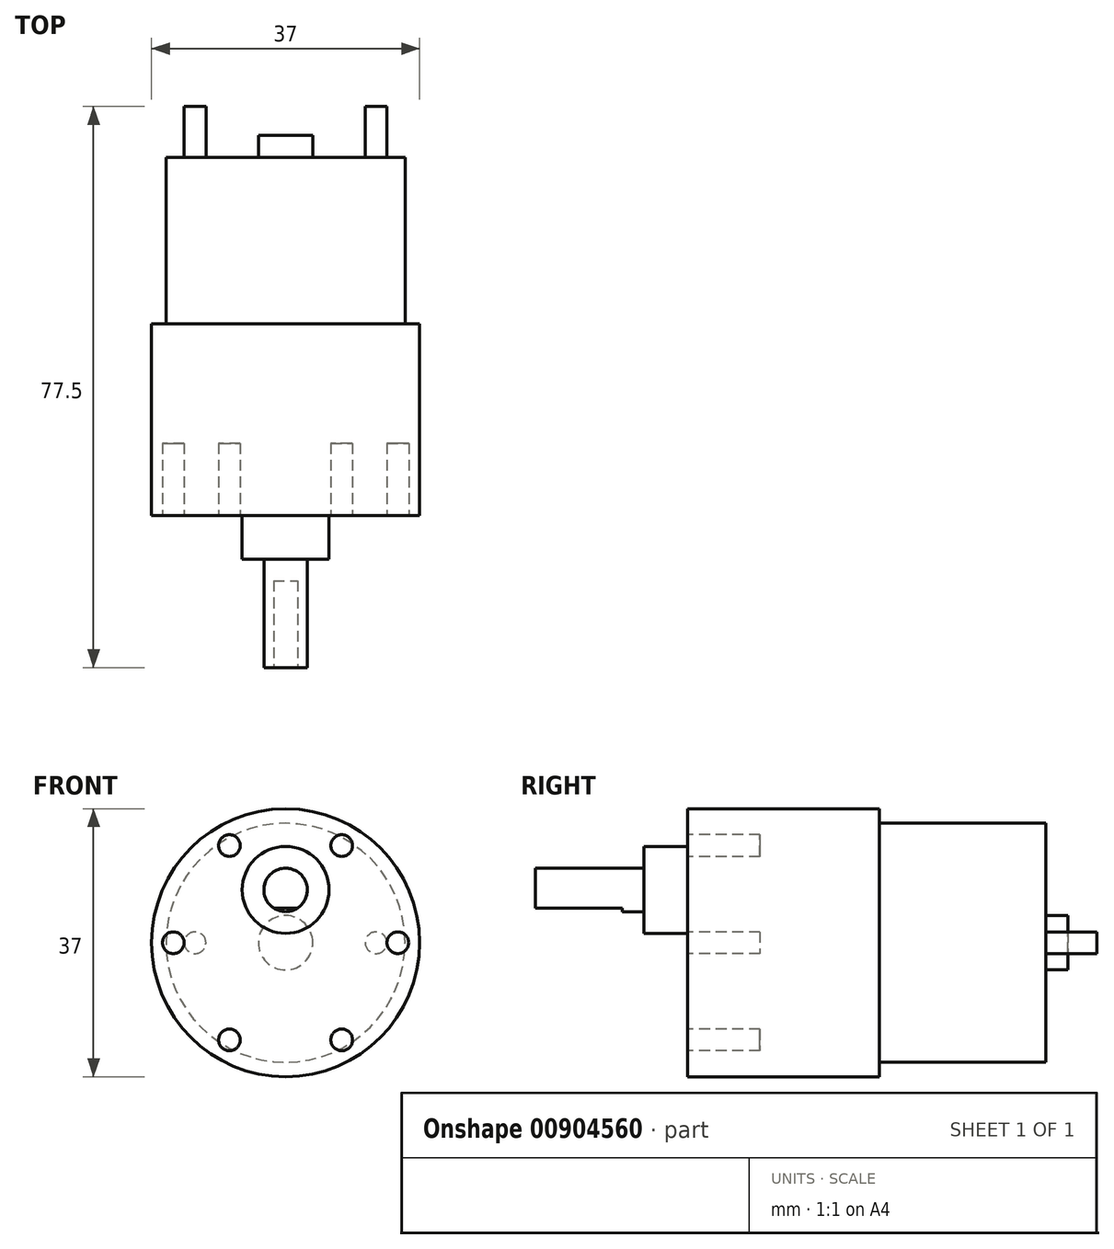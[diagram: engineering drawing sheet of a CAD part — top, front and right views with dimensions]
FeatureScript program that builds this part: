
annotation { "Feature Type Name" : "Feature", "Feature Type Description" : "" }
export const myFeature = defineFeature(function(context is Context, id is Id, definition is map)
    precondition{}
    {
        {
            var Q0;
            Q0=qCreatedBy(makeId("Front.planeOp"),FACE);
            var sketch = newSketch(context, id + "F0", { "sketchPlane" : qUnion([Q0])});
            skCircle(sketch, "E0", {"center": v(0, 0) * mm, "radius": 16.5 * mm});
            skCircle(sketch, "E1", {"center": v(0, 0) * mm, "radius": 18.5 * mm});
            skSolve(sketch);
        }
        {
            var Q0;
            Q0 = qSketchRegion(id + "F0", true);
            var Q1;
            Q1=makeQuery(id+"F0.imprint","IMPRINT",FACE,{"disambiguationData":[TD([[makeQuery(id+"F0.imprint","IMPRINT",EDGE,{"derivedFrom":sQuery(id+"F0.wireOp",EDGE,"E0")}),1.0]])]});
            extrude(context, id + "F1", {"entities" : qUnion([Q0, Q1]), "depth" : 26.5 * mm, "offsetDistance" : 25 * mm});
        }
        {
            var Q0;
            Q0=makeQuery(id+"F0.imprint","IMPRINT",FACE,{"disambiguationData":[TD([[makeQuery(id+"F0.imprint","IMPRINT",EDGE,{"derivedFrom":sQuery(id+"F0.wireOp",EDGE,"E0")}),1.0]])]});
            extrude(context, id + "F2", {"entities" : qUnion([Q0]), "operationType" : NewBodyOperationType.ADD, "oppositeDirection" : true, "depth" : 23 * mm, "offsetDistance" : 25 * mm});
        }
        {
            var Q0;
            Q0=makeQuery(id+"F1.opExtrude","CAP_FACE",FACE,{"disambiguationData":[OSD([sQuery(id+"F0.wireOp",EDGE,"E1")])],"isStart":false});
            var sketch = newSketch(context, id + "F3", { "sketchPlane" : qUnion([Q0])});
            skCircle(sketch, "E2", {"center": v(0, 7.3) * mm, "radius": 6 * mm});
            skCircle(sketch, "E3", {"center": v(0, 7.3) * mm, "radius": 3 * mm});
            skPoint(sketch, "E4", {"position": v(0, 1.3) * mm});
            skCircle(sketch, "E5", {"center": v(-15.5, 0) * mm, "radius": 1.5 * mm});
            skSolve(sketch);
        }
        {
            var Q0;
            Q0=makeQuery(id+"F3.imprint","IMPRINT",FACE,{"disambiguationData":[TD([[makeQuery(id+"F3.imprint","IMPRINT",EDGE,{"derivedFrom":sQuery(id+"F3.wireOp",EDGE,"E2")}),1.0]])]});
            extrude(context, id + "F4", {"entities" : qUnion([Q0]), "operationType" : NewBodyOperationType.ADD, "depth" : 6 * mm, "offsetDistance" : 25 * mm});
        }
        {
            var Q0;
            Q0=makeQuery(id+"F4.boolean.opBoolean","SPLIT",FACE,{"disambiguationData":[TD([makeQuery(id+"F4.opExtrude","SWEPT_FACE",FACE,{"disambiguationData":[OSD([sQuery(id+"F3.wireOp",EDGE,"E3")])]})])],"derivedFrom":makeQuery(id+"F1.opExtrude","CAP_FACE",FACE,{"disambiguationData":[OSD([sQuery(id+"F0.wireOp",EDGE,"E1")])],"isStart":false})});
            extrude(context, id + "F5", {"entities" : qUnion([Q0]), "operationType" : NewBodyOperationType.ADD, "depth" : 21 * mm, "offsetDistance" : 25 * mm});
        }
        {
            var Q0;
            Q0=makeQuery(id+"F5.opExtrude","CAP_FACE",FACE,{"disambiguationData":[OSD([sQuery(id+"F0.wireOp",EDGE,"E1")])],"isStart":false});
            var sketch = newSketch(context, id + "F6", { "sketchPlane" : qUnion([Q0])});
            skLineSegment(sketch, "E6", {"start": v(-1.66, 4.8) * mm, "end": v(1.66, 4.8) * mm});
            skArc(sketch, "E7", {"start": v(-1.66, 4.8) * mm, "mid": v(0, 4.3) * mm, "end": v(1.66, 4.8) * mm});
            skSolve(sketch);
        }
        {
            var Q0;
            Q0=makeQuery(id+"F6.imprint","IMPRINT",FACE,{"disambiguationData":[TD([[makeQuery(id+"F6.imprint","IMPRINT",EDGE,{"derivedFrom":sQuery(id+"F6.wireOp",EDGE,"E6")}),-1.0]])]});
            extrude(context, id + "F7", {"entities" : qUnion([Q0]), "operationType" : NewBodyOperationType.REMOVE, "oppositeDirection" : true, "depth" : 12 * mm, "offsetDistance" : 25 * mm});
        }
        {
            var Q0;
            Q0=makeQuery(id+"F3.imprint","IMPRINT",FACE,{"disambiguationData":[TD([[makeQuery(id+"F3.imprint","IMPRINT",EDGE,{"derivedFrom":sQuery(id+"F3.wireOp",EDGE,"E5")}),1.0]])]});
            var Q1;
            Q1=sQuery(id+"F3.wireOp",EDGE,"E5");
            extrude(context, id + "F8", {"entities" : qUnion([Q0]), "surfaceEntities" : qUnion([Q1]), "oppositeDirection" : true, "depth" : 10 * mm, "offsetDistance" : 25 * mm});
        }
        {
            var Q0;
            Q0=qCreatedBy(makeId("Right.planeOp"),FACE);
            var sketch = newSketch(context, id + "F9", { "sketchPlane" : qUnion([Q0])});
            skLineSegment(sketch, "E8", {"start": v(-66.54, 0) * mm, "end": v(54.78, 0) * mm, "construction": true});
            skSolve(sketch);
        }
        {
            var Q0;
            Q0=makeQuery(id+"F8.opExtrude","SWEPT_BODY",BODY,{"disambiguationData":[OSD([sQuery(id+"F3.wireOp",EDGE,"E5")])]});
            var Q1;
            Q1=sQuery(id+"F9.wireOp",EDGE,"E8");
            circularPattern(context, id + "F10", {"operationType" : NewBodyOperationType.REMOVE, "entities" : qUnion([Q0]), "axis" : qUnion([Q1]), "angle" : 360 * degree, "instanceCount" : 6, "equalSpace" : true});
        }
        {
            var Q0;
            Q0=makeQuery(id+"F2.opExtrude","CAP_FACE",FACE,{"disambiguationData":[OSD([sQuery(id+"F0.wireOp",EDGE,"E0")])],"isStart":false});
            var sketch = newSketch(context, id + "F11", { "sketchPlane" : qUnion([Q0])});
            skCircle(sketch, "E9", {"center": v(0, 0) * mm, "radius": 3.75 * mm});
            skCircle(sketch, "E10", {"center": v(-12.5, 0) * mm, "radius": 1.5 * mm});
            skCircle(sketch, "E11", {"center": v(12.5, 0) * mm, "radius": 1.5 * mm});
            skSolve(sketch);
        }
        {
            var Q0;
            Q0 = qSketchRegion(id + "F11", true);
            extrude(context, id + "F12", {"entities" : qUnion([Q0]), "operationType" : NewBodyOperationType.ADD, "depth" : 3 * mm, "offsetDistance" : 25 * mm});
        }
        {
            var Q0;
            Q0=makeQuery(id+"F11.imprint","IMPRINT",FACE,{"disambiguationData":[TD([[makeQuery(id+"F11.imprint","IMPRINT",EDGE,{"derivedFrom":sQuery(id+"F11.wireOp",EDGE,"E10")}),1.0]])]});
            var Q1;
            Q1=makeQuery(id+"F11.imprint","IMPRINT",FACE,{"disambiguationData":[TD([[makeQuery(id+"F11.imprint","IMPRINT",EDGE,{"derivedFrom":sQuery(id+"F11.wireOp",EDGE,"E11")}),1.0]])]});
            extrude(context, id + "F13", {"entities" : qUnion([Q0, Q1]), "operationType" : NewBodyOperationType.ADD, "depth" : 7 * mm, "offsetDistance" : 25 * mm});
        }
    });
